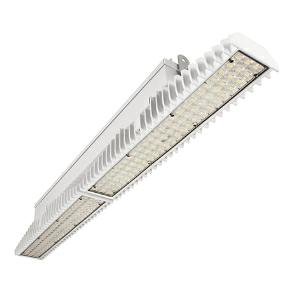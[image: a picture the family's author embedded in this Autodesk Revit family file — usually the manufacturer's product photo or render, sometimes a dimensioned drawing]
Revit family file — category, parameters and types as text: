
# Revit family: 3f_filippi_-_3f_lem_medio_3f_filippi_-_58896_a0811_-_3f_lem_1_1_led_100_cr_medio___vt_269d
name_source: partatom
category: Lighting Fixtures
units: mm (PartAtom-declared; Revit-internal decimal feet)

## family parameters
Cut with Voids When Loaded = No
Host = Face
Light Source = No
Part Type = Normal
Room Calculation Point = No
Round Connector Dimension = Use Diameter
Shared = No

## types (1)
- 3F Filippi - 3F LEM Medio (1 x LED, 15479 lm, 109 W, 4000 K)
    Apparent Load = 109 VA
    Approval mark = CE
    CIE Flux Codes = 83 96 99 100 100
    Color Rendering = 80
    Color Temperature = 4000 K
    Control Gear = Electronic ballast
    Default Elevation = 1800 mm
    Description = Industrial luminaire with high light output and high luminous efficiency designed with the most innovative technologies for environments with temperature up to 55°C.

ILLUMINOTECHNICAL
Luminous efficiency 100% (DLOR 99%, ULOR 1%).
Initial luminous flux of the luminaire 15479 lm.
Medium distribution with rectangular shape.
Installation Interdistance Transv.D = 1.02 x hu - Long.D = 1.06 x hu.
Tabular UGR (CIE 117 - 4H-8H; S=0.25H; 70/50/20): RUG 21.9 - 21.4.
Beam angle: 65° - 67°.
Luminous efficacy 142 lm/W.
Lifetime (L93/B10): 30000 h. (tq+25°C)
Lifetime (L90/B10): 50000 h. (tq+25°C)
Lifetime (L85/B10): 80000 h. (tq+25°C)
Lifetime (L80/B10): 100000 h. (tq+25°C)
Lifetime (L85/B10): 50000 h. (tq+55°C)
Sudden decreased luminous flux after 50000 hours: 0% (C0).
Photobiological safety in compliance with IEC/TR 62778: RG0 risk exempt, (IEC 62471).
In compliance with IEC/EN 62722-2-1 - IEC/EN 62717 standards.

SOURCE
2 Mid-Power linear LED modules 50W/840.
Energy efficiency class (UE 2019/2020 - UE 2019/2015): C.
CIE 13.3 Colour rendering index: CRI >80 (R9 <50%).
IES TM-30 Fidelity Index: Rf = 84 Rg = 95.
CCT nominal colour temperature 4000 K.
Colour initial tolerance (MacAdam): SDCM 3.

MECHANICAL
Passive modular heatsinks in die-casted aluminium, painted in white colour.
To optimize the thermal management of the LED module, the heatsinks are oversized and provided with self-cleaning of cooling fins.
Wiring body in aluminium and galvanised steel anchored solidly to the sinks and thermally separated.
3F Lens lenses with high luminous efficiency, transparent methacrylate (PMMA), fixed to the LED modules.
Fixing brackets in stainless steel.
Luminaire with limited surface temperature. - D - (EN 60598-2-24)
Dimensions: 1099x115 mm, height 154 mm. Weight 11.334 kg.
IP65 protection degree.
Mechanical strength to impacts IK06 (1 joule).
Glow-wire test resistance 650°C.

ELECTRICAL
Halogen Free electronic wiring 230V-50/60Hz, power factor 0.97, THD <25%, constant output current, class I, 1 driver.
Power of the luminaire 109 W.
ENEC - CE.
SAFE FLICKER: PstLM=<1 and SVM=<0.4 (IEC TR 61547-1 and IEC TR 63158), to ensure a more comfortable and safe light.
Luminaire compliant with EN 60598-2-22 for power supply from a centralised emergency system CPSS (Central Power Supply System), not incorporated in the luminaire - high risk areas excluded. The default power and flux are 100% in AC and 100% in DC.
Ambient temperature from -30°C to +55°C.
Temperature class T6 max 85°C.
Quick connection via M20 3P connector with 9-13 mm tightening range.
Power unit positioned on a separate compartment by the LED module to ensure optimum temperatures of cabling components, to be inspectable and maintainable.
Relative humidity UR: <85%.

INSTALLATION
Ceiling / Suspended / Wall.
All accessories dedicated to this product are available on the Catalog and on our website www.3F-Filippi.com.

ACCESSORIES
A0811 - VT transparent glass, tempered, not flammable, with sealing gasket.
One required for each light module. The pack contains 10 pieces.

APPLICATIONS
In commercial environments, exhibition and industrial areas, stores, open areas.
Applications with high ambient temperature up to 55°C.
Environments in which it is necessary a total protection against falling fragments (eg environments with foodstuffs or machines with moving parts or with extreme temperature changes), use luminaires with polycarbonate lenses.

WARNING
Fixture not suitable for cold stores with an ambient temperature <0°C and/or relative humidity >85%.
Luminaire designed for disposal/recycling at end-of-life.
Replaceable (LED only) light source by a professional. Replaceable control gear by a professional.
    Height = 154 mm
    Lamp = 1 x LED
    Lamp Light Flux = 15479 lm
    Lamp Power = 109 W
    Lamp count = 1
    Length = 1099 mm
    Lifetime = 50000 h
    Luminous efficacy = 142 lm/W
    Manufacturer = 3F Filippi
    ModVariant = No
    Model = 3F Filippi - 58896+A0811 - 3F LEM 1+1 LED 100 CR MEDIO + VT
    Mounting Place = Ceiling
    Mounting Type = Pendant
    Number of Poles = 1
    OnlyDefault = Yes
    Power Factor = 1
    Product Name = 3F Filippi - 3F LEM Medio
    Product group = pendant luminaire
    ProductGroupID = 9
    Protection Class = Protection class I
    Protection Degree = IP 65
    RLX_Detail_Level = 1
    RLX_Emergency_Light_Flux = 0 lm
    RLX_Emergency_Type = 0
    RLX_Emergency_Type_DB = No
    RlxData = <blob elided: 97677 chars, md5=582a12ef>
    Socket = socket
    Standby Power = 0 W
    System Light Flux = 15479 lm
    System Power = 109 W
    Type Comments = Product without accessories
    Type Image = 3f_filippi_-_lem_11__a0811.jpg
    URL = http://relux.com
    VarID = ---
    Voltage = 0 V
    Weight = 0.00 kg
    Width = 115 mm

## geometry (parser evidence)
native form markers: Blend x4, Sweep x11
no freeform markers — native parametric forms only
